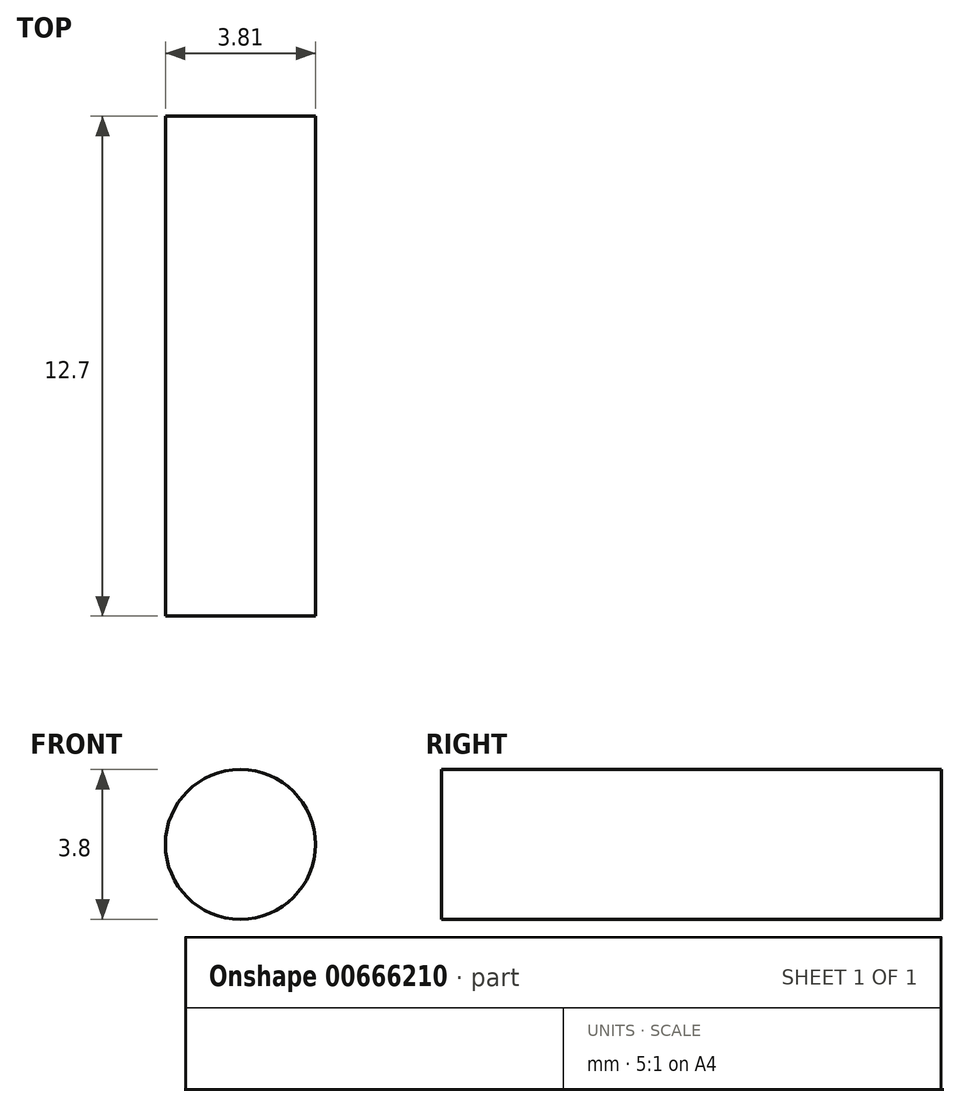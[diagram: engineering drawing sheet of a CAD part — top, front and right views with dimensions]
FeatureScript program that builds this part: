
annotation { "Feature Type Name" : "Feature", "Feature Type Description" : "" }
export const myFeature = defineFeature(function(context is Context, id is Id, definition is map)
    precondition{}
    {
        {
            var Q0;
            Q0=qCreatedBy(makeId("Front.planeOp"),FACE);
            var sketch = newSketch(context, id + "F0", { "sketchPlane" : qUnion([Q0])});
            skLineSegment(sketch, "E0.bottom", {"start": v(18.61, -4.4) * mm, "end": v(10.26, -4.4) * mm});
            skLineSegment(sketch, "E0.top", {"start": v(18.61, 4.4) * mm, "end": v(-18.61, 4.4) * mm});
            skLineSegment(sketch, "E0.left", {"start": v(18.61, -4.4) * mm, "end": v(18.61, 4.4) * mm});
            skLineSegment(sketch, "E0.right", {"start": v(-18.61, -4.4) * mm, "end": v(-18.61, 4.4) * mm});
            skPoint(sketch, "E0.middle", {"position": v(0, 0) * mm});
            skArc(sketch, "E1", {"start": v(-10.26, -4.4) * mm, "mid": v(0, -14.66) * mm, "end": v(10.26, -4.4) * mm});
            skLineSegment(sketch, "E2.trimOffspring", {"start": v(-10.26, -4.4) * mm, "end": v(-18.61, -4.4) * mm});
            skSolve(sketch);
        }
        {
            var Q0;
            Q0=makeQuery(id+"F0.imprint","IMPRINT",FACE,{"disambiguationData":[TD([[makeQuery(id+"F0.imprint","IMPRINT",EDGE,{"derivedFrom":sQuery(id+"F0.wireOp",EDGE,"E0.bottom")}),-1.0]])]});
            extrude(context, id + "F1", {"entities" : qUnion([Q0]), "depth" : 6.35 * mm, "offsetDistance" : 25.4 * mm, "hasSecondDirection" : true, "secondDirectionOppositeDirection" : true, "secondDirectionDepth" : 6.35 * mm});
        }
        {
            var Q0;
            Q0=makeQuery(id+"F1.opExtrude","CAP_FACE",FACE,{"disambiguationData":[OSD([sQuery(id+"F0.wireOp",EDGE,"E0.bottom"),sQuery(id+"F0.wireOp",EDGE,"E0.top"),sQuery(id+"F0.wireOp",EDGE,"E0.left"),sQuery(id+"F0.wireOp",EDGE,"E0.right"),sQuery(id+"F0.wireOp",EDGE,"E1"),sQuery(id+"F0.wireOp",EDGE,"E2.trimOffspring")])],"isStart":false});
            var sketch = newSketch(context, id + "F2", { "sketchPlane" : qUnion([Q0])});
            skCircle(sketch, "E3", {"center": v(-15.43, 0) * mm, "radius": 1.9 * mm});
            skCircle(sketch, "E4.MirrorC", {"center": v(15.43, 0) * mm, "radius": 1.9 * mm});
            skSolve(sketch);
        }
        {
            var Q0;
            Q0=makeQuery(id+"F2.imprint","IMPRINT",FACE,{"disambiguationData":[TD([[makeQuery(id+"F2.imprint","IMPRINT",EDGE,{"derivedFrom":sQuery(id+"F2.wireOp",EDGE,"E3")}),1.0]])]});
            var Q1;
            Q1=sQuery(id+"F2.wireOp",EDGE,"E3");
            extrude(context, id + "F3", {"entities" : qUnion([Q0]), "operationType" : NewBodyOperationType.REMOVE, "surfaceEntities" : qUnion([Q1]), "oppositeDirection" : true, "depth" : 15.36 * mm, "offsetDistance" : 25.4 * mm});
        }
        {
            var Q0;
            Q0=makeQuery(id+"F2.imprint","IMPRINT",FACE,{"disambiguationData":[TD([[makeQuery(id+"F2.imprint","IMPRINT",EDGE,{"derivedFrom":sQuery(id+"F2.wireOp",EDGE,"E4.MirrorC")}),-1.0]])]});
            extrude(context, id + "F4", {"entities" : qUnion([Q0]), "operationType" : NewBodyOperationType.REMOVE, "oppositeDirection" : true, "depth" : 14.15 * mm, "offsetDistance" : 25.4 * mm});
        }
        {
            var Q0;
            Q0=makeQuery(id+"F2.imprint","IMPRINT",FACE,{"disambiguationData":[TD([[makeQuery(id+"F2.imprint","IMPRINT",EDGE,{"derivedFrom":sQuery(id+"F2.wireOp",EDGE,"E3")}),-1.0]])]});
            var sketch = newSketch(context, id + "F5", { "sketchPlane" : qUnion([Q0])});
            skCircle(sketch, "E5", {"center": v(0, -7.07) * mm, "radius": 5.7 * mm});
            skSolve(sketch);
        }
        {
            var Q0;
            Q0=makeQuery(id+"F5.imprint","IMPRINT",FACE,{"disambiguationData":[TD([[makeQuery(id+"F5.imprint","IMPRINT",EDGE,{"derivedFrom":sQuery(id+"F5.wireOp",EDGE,"E5")}),1.0]])]});
            extrude(context, id + "F6", {"entities" : qUnion([Q0]), "operationType" : NewBodyOperationType.REMOVE, "oppositeDirection" : true, "depth" : 15.33 * mm, "offsetDistance" : 25.4 * mm});
        }
    });
